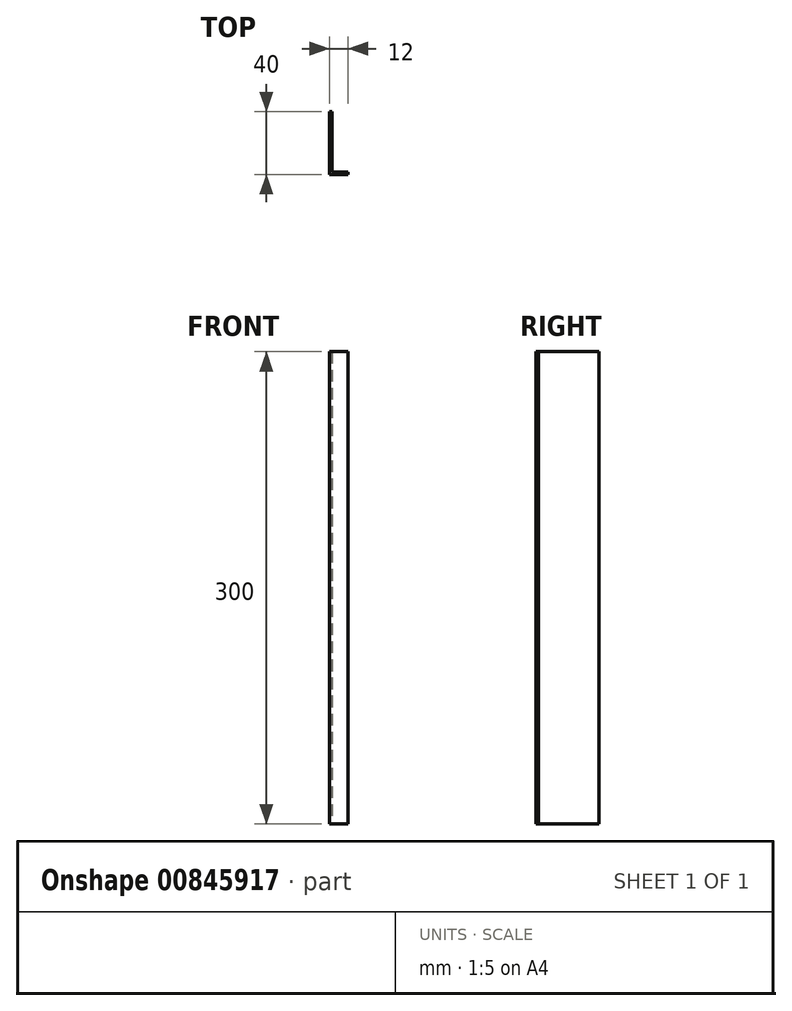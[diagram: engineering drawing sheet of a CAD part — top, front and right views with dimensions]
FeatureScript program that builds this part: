
annotation { "Feature Type Name" : "Feature", "Feature Type Description" : "" }
export const myFeature = defineFeature(function(context is Context, id is Id, definition is map)
    precondition{}
    {
        {
            var Q0;
            Q0=qCreatedBy(makeId("Top.planeOp"),FACE);
            var sketch = newSketch(context, id + "F0", { "sketchPlane" : qUnion([Q0])});
            skLineSegment(sketch, "E0", {"start": v(-2, -28.74) * mm, "end": v(10, -28.74) * mm});
            skLineSegment(sketch, "E1", {"start": v(10, -28.74) * mm, "end": v(10, -27.14) * mm});
            skLineSegment(sketch, "E2", {"start": v(10, -27.14) * mm, "end": v(-0.4, -27.14) * mm});
            skLineSegment(sketch, "E3", {"start": v(-0.4, -27.14) * mm, "end": v(-0.4, 11.26) * mm});
            skLineSegment(sketch, "E4", {"start": v(-0.4, 11.26) * mm, "end": v(-2, 11.26) * mm});
            skLineSegment(sketch, "E5", {"start": v(-2, 11.26) * mm, "end": v(-2, -28.74) * mm});
            skSolve(sketch);
        }
        {
            var Q0;
            Q0=makeQuery(id+"F0.imprint","IMPRINT",FACE,{"disambiguationData":[TD([[makeQuery(id+"F0.imprint","IMPRINT",EDGE,{"derivedFrom":sQuery(id+"F0.wireOp",EDGE,"E0")}),1.0]])]});
            extrude(context, id + "F1", {"entities" : qUnion([Q0]), "depth" : 300 * mm, "offsetDistance" : 25 * mm});
        }
    });
